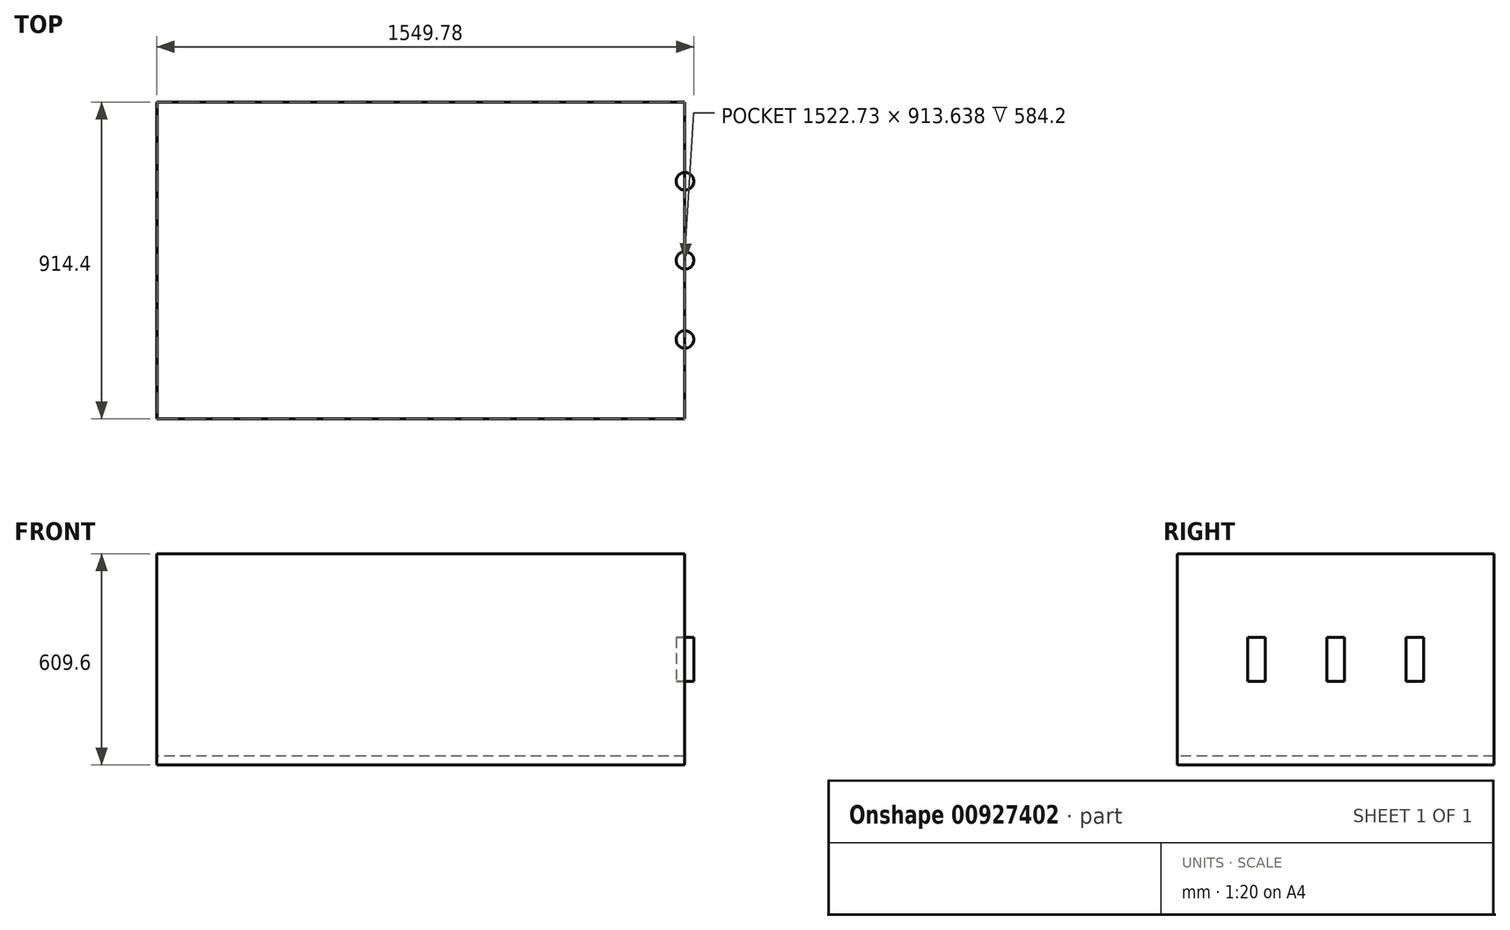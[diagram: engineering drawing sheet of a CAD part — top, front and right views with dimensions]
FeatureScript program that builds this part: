
annotation { "Feature Type Name" : "Feature", "Feature Type Description" : "" }
export const myFeature = defineFeature(function(context is Context, id is Id, definition is map)
    precondition{}
    {
        {
            var Q0;
            Q0=qCreatedBy(makeId("Top.planeOp"),FACE);
            var sketch = newSketch(context, id + "F0", { "sketchPlane" : qUnion([Q0])});
            skLineSegment(sketch, "E0.bottom", {"start": v(-67.56, -71.67) * mm, "end": v(1456.44, -71.67) * mm});
            skLineSegment(sketch, "E0.top", {"start": v(-67.56, 842.73) * mm, "end": v(1456.44, 842.73) * mm});
            skLineSegment(sketch, "E0.left", {"start": v(-67.56, -71.67) * mm, "end": v(-67.56, 842.73) * mm});
            skLineSegment(sketch, "E0.right", {"start": v(1456.44, -71.67) * mm, "end": v(1456.44, 842.73) * mm});
            skSolve(sketch);
        }
        {
            var Q0;
            Q0=makeQuery(id+"F0.imprint","IMPRINT",FACE,{"disambiguationData":[TD([[makeQuery(id+"F0.imprint","IMPRINT",EDGE,{"derivedFrom":sQuery(id+"F0.wireOp",EDGE,"E0.bottom")}),1.0]])]});
            var sketch = newSketch(context, id + "F1", { "sketchPlane" : qUnion([Q0])});
            skLineSegment(sketch, "E1.0", {"start": v(-67.56, -71.67) * mm, "end": v(-67.56, 842.73) * mm});
            skLineSegment(sketch, "E2.0", {"start": v(1456.44, -71.67) * mm, "end": v(1456.44, 842.73) * mm});
            skLineSegment(sketch, "E3.bottom", {"start": v(1455.8, 842.34) * mm, "end": v(-66.92, 842.34) * mm});
            skLineSegment(sketch, "E3.top", {"start": v(1455.8, -71.3) * mm, "end": v(-66.92, -71.3) * mm});
            skLineSegment(sketch, "E3.left", {"start": v(1455.8, 842.34) * mm, "end": v(1455.8, -71.3) * mm});
            skLineSegment(sketch, "E3.right", {"start": v(-66.92, 842.34) * mm, "end": v(-66.92, -71.3) * mm});
            skPoint(sketch, "E3.middle", {"position": v(694.44, 385.53) * mm});
            skSolve(sketch);
        }
        {
            var Q0;
            Q0=makeQuery(id+"F1.imprint","IMPRINT",FACE,{"disambiguationData":[TD([[makeQuery(id+"F1.imprint","IMPRINT",EDGE,{"derivedFrom":sQuery(id+"F1.wireOp",EDGE,"E1.0")}),-1.0]])]});
            extrude(context, id + "F2", {"entities" : qUnion([Q0]), "depth" : 609.6 * mm, "offsetDistance" : 25.4 * mm});
        }
        {
            var Q0;
            Q0 = qSketchRegion(id + "F1", true);
            var Q1;
            Q1 = qSketchRegion(id + "F0", true);
            extrude(context, id + "F3", {"entities" : qUnion([Q0, Q1]), "operationType" : NewBodyOperationType.ADD, "depth" : 25.4 * mm, "offsetDistance" : 25.4 * mm});
        }
        {
            var Q0;
            Q0=makeQuery(id+"F2.opExtrude","CAP_VERTEX",VERTEX,{"disambiguationData":[OSD([sQuery(id+"F1.wireOp",EDGE,"E3.bottom"),sQuery(id+"F1.wireOp",EDGE,"E3.left")])],"isStart":false});
            var Q1;
            Q1=makeQuery(id+"F2.opExtrude","CAP_VERTEX",VERTEX,{"disambiguationData":[OSD([sQuery(id+"F0.wireOp",EDGE,"E0.top"),sQuery(id+"F1.wireOp",EDGE,"E2.0")])],"isStart":true});
            cPlane(context, id + "F4", {"entities" : qUnion([Q0, Q1]), "cplaneType" : CPlaneType.MID_PLANE, "offset" : 25.4 * mm, "width" : 152.4 * mm, "height" : 152.4 * mm});
        }
        {
            var Q0;
            Q0=qCreatedBy(id+"F4.planeOp",FACE);
            var sketch = newSketch(context, id + "F5", { "sketchPlane" : qUnion([Q0])});
            skLineSegment(sketch, "E4.0", {"start": v(-66.92, -843.1) * mm, "end": v(1457.07, -843.1) * mm});
            skLineSegment(sketch, "E5.0", {"start": v(1456.44, 70.91) * mm, "end": v(-66.29, 70.91) * mm});
            skLineSegment(sketch, "E6.0", {"start": v(1457.08, 71.3) * mm, "end": v(1457.07, -843.1) * mm});
            skCircle(sketch, "E7", {"center": v(1457.07, -614.5) * mm, "radius": 25.4 * mm});
            skCircle(sketch, "E8", {"center": v(1457.07, -157.69) * mm, "radius": 25.4 * mm});
            skCircle(sketch, "E9", {"center": v(1457.07, -386.1) * mm, "radius": 25.4 * mm});
            skLineSegment(sketch, "E10", {"start": v(1457.07, -614.5) * mm, "end": v(1457.07, -386.1) * mm});
            skLineSegment(sketch, "E11", {"start": v(1457.07, -386.1) * mm, "end": v(1457.07, -157.69) * mm});
            skSolve(sketch);
        }
        {
            var Q0;
            {var subQ0=sQuery(id+"F5.wireOp",EDGE,"E11");var subQ1=sQuery(id+"F5.wireOp",EDGE,"E6.0");var subQ2=makeQuery(id+"F5.imprint","INTERSECT",VERTEX,{"derivedFrom":[subQ1,subQ0]});Q0=makeQuery(id+"F5.imprint","IMPRINT",FACE,{"disambiguationData":[TD([[makeQuery(id+"F5.imprint","IMPRINT",EDGE,{"disambiguationData":[TD([[subQ2,1.0]])],"derivedFrom":subQ1}),1.0]])]});}
            var Q1;
            {var subQ0=sQuery(id+"F5.wireOp",EDGE,"E10");var subQ1=sQuery(id+"F5.wireOp",EDGE,"E9");var subQ2=makeQuery(id+"F5.imprint","INTERSECT",VERTEX,{"derivedFrom":[subQ1,subQ0]});Q1=makeQuery(id+"F5.imprint","IMPRINT",FACE,{"disambiguationData":[TD([[makeQuery(id+"F5.imprint","IMPRINT",EDGE,{"disambiguationData":[TD([[subQ2,-1.0]])],"derivedFrom":subQ1}),1.0]])]});}
            var Q2;
            {var subQ0=sQuery(id+"F5.wireOp",EDGE,"E10");var subQ1=sQuery(id+"F5.wireOp",EDGE,"E6.0");var subQ2=makeQuery(id+"F5.imprint","INTERSECT",VERTEX,{"derivedFrom":[subQ1,subQ0]});Q2=makeQuery(id+"F5.imprint","IMPRINT",FACE,{"disambiguationData":[TD([[makeQuery(id+"F5.imprint","IMPRINT",EDGE,{"disambiguationData":[TD([[subQ2,-1.0]])],"derivedFrom":subQ1}),1.0]])]});}
            var Q3;
            {var subQ0=sQuery(id+"F5.wireOp",EDGE,"E10");var subQ1=sQuery(id+"F5.wireOp",EDGE,"E6.0");var subQ2=makeQuery(id+"F5.imprint","INTERSECT",VERTEX,{"derivedFrom":[subQ1,subQ0]});Q3=makeQuery(id+"F5.imprint","IMPRINT",FACE,{"disambiguationData":[TD([[makeQuery(id+"F5.imprint","IMPRINT",EDGE,{"disambiguationData":[TD([[subQ2,-1.0]])],"derivedFrom":subQ1}),-1.0]])]});}
            var Q4;
            {var subQ0=sQuery(id+"F5.wireOp",EDGE,"E10");var subQ1=sQuery(id+"F5.wireOp",EDGE,"E9");var subQ2=makeQuery(id+"F5.imprint","INTERSECT",VERTEX,{"derivedFrom":[subQ1,subQ0]});Q4=makeQuery(id+"F5.imprint","IMPRINT",FACE,{"disambiguationData":[TD([[makeQuery(id+"F5.imprint","IMPRINT",EDGE,{"disambiguationData":[TD([[subQ2,1.0]])],"derivedFrom":subQ1}),1.0]])]});}
            var Q5;
            {var subQ0=sQuery(id+"F5.wireOp",EDGE,"E11");var subQ1=sQuery(id+"F5.wireOp",EDGE,"E6.0");var subQ2=makeQuery(id+"F5.imprint","INTERSECT",VERTEX,{"derivedFrom":[subQ1,subQ0]});Q5=makeQuery(id+"F5.imprint","IMPRINT",FACE,{"disambiguationData":[TD([[makeQuery(id+"F5.imprint","IMPRINT",EDGE,{"disambiguationData":[TD([[subQ2,1.0]])],"derivedFrom":subQ1}),-1.0]])]});}
            extrude(context, id + "F6", {"entities" : qUnion([Q0, Q1, Q2, Q3, Q4, Q5]), "operationType" : NewBodyOperationType.ADD, "endBound" : BoundingType.SYMMETRIC, "oppositeDirection" : true, "depth" : 127 * mm, "offsetDistance" : 25.4 * mm});
        }
    });
